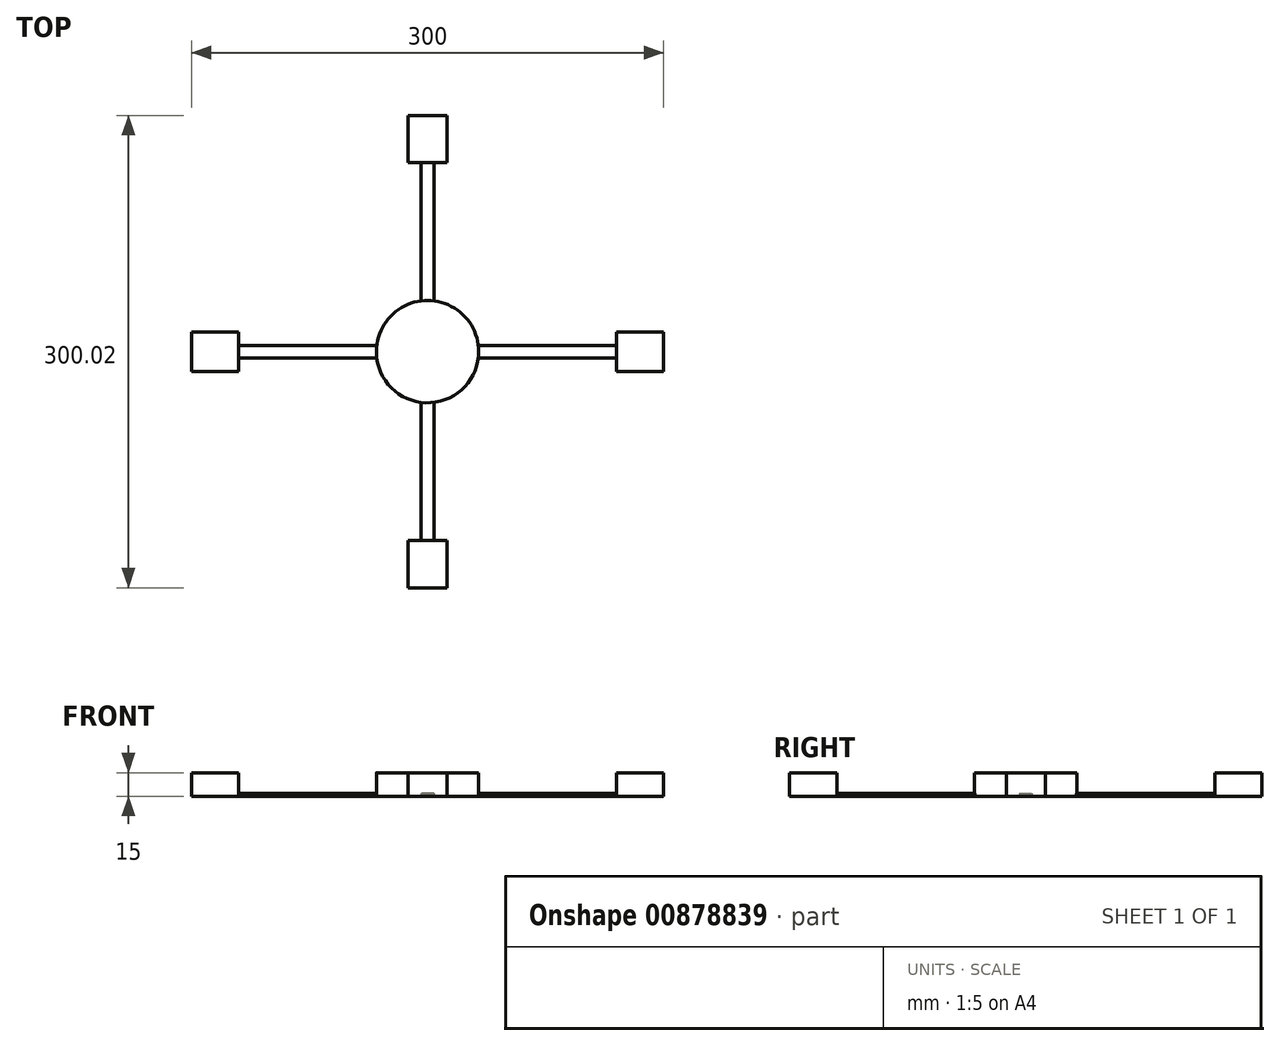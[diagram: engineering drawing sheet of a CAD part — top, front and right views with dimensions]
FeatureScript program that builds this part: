
annotation { "Feature Type Name" : "Feature", "Feature Type Description" : "" }
export const myFeature = defineFeature(function(context is Context, id is Id, definition is map)
    precondition{}
    {
        {
            var Q0;
            Q0=qCreatedBy(makeId("Top.planeOp"),FACE);
            var sketch = newSketch(context, id + "F0", { "sketchPlane" : qUnion([Q0])});
            skLineSegment(sketch, "E0.bottom", {"start": v(-120, -12.5) * mm, "end": v(-150, -12.5) * mm});
            skLineSegment(sketch, "E0.top", {"start": v(-120, 12.5) * mm, "end": v(-150, 12.5) * mm});
            skLineSegment(sketch, "E0.left", {"start": v(-120, -12.5) * mm, "end": v(-120, -4) * mm});
            skLineSegment(sketch, "E0.right", {"start": v(-150, -12.5) * mm, "end": v(-150, 12.5) * mm});
            skPoint(sketch, "E0.middle", {"position": v(-135, 0) * mm});
            skLineSegment(sketch, "E1.bottom", {"start": v(12.5, 150.02) * mm, "end": v(-12.5, 150.02) * mm});
            skLineSegment(sketch, "E1.top", {"start": v(12.5, 120.02) * mm, "end": v(4, 120.02) * mm});
            skLineSegment(sketch, "E1.left", {"start": v(12.5, 150.02) * mm, "end": v(12.5, 120.02) * mm});
            skLineSegment(sketch, "E1.right", {"start": v(-12.5, 150.02) * mm, "end": v(-12.5, 120.02) * mm});
            skPoint(sketch, "E1.middle", {"position": v(0, 135.02) * mm});
            skLineSegment(sketch, "E2.bottom", {"start": v(150, -12.5) * mm, "end": v(120, -12.5) * mm});
            skLineSegment(sketch, "E2.top", {"start": v(150, 12.5) * mm, "end": v(120, 12.5) * mm});
            skLineSegment(sketch, "E2.left", {"start": v(150, -12.5) * mm, "end": v(150, 12.5) * mm});
            skLineSegment(sketch, "E2.right", {"start": v(120, -12.5) * mm, "end": v(120, -4) * mm});
            skPoint(sketch, "E2.middle", {"position": v(135, 0) * mm});
            skLineSegment(sketch, "E3.bottom", {"start": v(12.5, -150) * mm, "end": v(-12.5, -150) * mm});
            skLineSegment(sketch, "E3.top", {"start": v(12.5, -120) * mm, "end": v(4, -120) * mm});
            skLineSegment(sketch, "E3.left", {"start": v(12.5, -150) * mm, "end": v(12.5, -120) * mm});
            skLineSegment(sketch, "E3.right", {"start": v(-12.5, -150) * mm, "end": v(-12.5, -120) * mm});
            skPoint(sketch, "E3.middle", {"position": v(0, -135) * mm});
            skArc(sketch, "E4", {"start": v(4, -32.25) * mm, "mid": v(22.98, -22.98) * mm, "end": v(32.25, -4) * mm});
            skLineSegment(sketch, "E5.left", {"start": v(4, 32.25) * mm, "end": v(4, 120.02) * mm});
            skLineSegment(sketch, "E5.right", {"start": v(-4, 32.25) * mm, "end": v(-4, 120.02) * mm});
            skLineSegment(sketch, "E6.bottom", {"start": v(120, -4) * mm, "end": v(32.25, -4) * mm});
            skLineSegment(sketch, "E6.top", {"start": v(120, 4) * mm, "end": v(32.25, 4) * mm});
            skLineSegment(sketch, "E7.bottom", {"start": v(-32.25, -4) * mm, "end": v(-120, -4) * mm});
            skLineSegment(sketch, "E7.top", {"start": v(-32.25, 4) * mm, "end": v(-120, 4) * mm});
            skLineSegment(sketch, "E8.left", {"start": v(4, -32.25) * mm, "end": v(4, -120) * mm});
            skLineSegment(sketch, "E8.right", {"start": v(-4, -32.25) * mm, "end": v(-4, -120) * mm});
            skLineSegment(sketch, "E9.trimOffspring", {"start": v(-4, 120.02) * mm, "end": v(-12.5, 120.02) * mm});
            skArc(sketch, "E10.trimOffspring", {"start": v(-32.25, -4) * mm, "mid": v(-22.98, -22.98) * mm, "end": v(-4, -32.25) * mm});
            skArc(sketch, "E11.trimOffspring", {"start": v(32.25, 4) * mm, "mid": v(22.98, 22.98) * mm, "end": v(4, 32.25) * mm});
            skLineSegment(sketch, "E12.trimOffspring", {"start": v(-120, 4) * mm, "end": v(-120, 12.5) * mm});
            skLineSegment(sketch, "E13.trimOffspring", {"start": v(-4, -120) * mm, "end": v(-12.5, -120) * mm});
            skArc(sketch, "E14.trimOffspring", {"start": v(-4, 32.25) * mm, "mid": v(-22.98, 22.98) * mm, "end": v(-32.25, 4) * mm});
            skLineSegment(sketch, "E15.trimOffspring", {"start": v(120, 4) * mm, "end": v(120, 12.5) * mm});
            skSolve(sketch);
        }
        {
            var Q0;
            Q0=makeQuery(id+"F0.imprint","IMPRINT",FACE,{"disambiguationData":[TD([[makeQuery(id+"F0.imprint","IMPRINT",EDGE,{"derivedFrom":sQuery(id+"F0.wireOp",EDGE,"E0.bottom")}),-1.0]])]});
            extrude(context, id + "F1", {"entities" : qUnion([Q0]), "depth" : 2 * mm, "offsetDistance" : 25 * mm});
        }
        {
            var Q0;
            Q0=makeQuery(id+"F1.opExtrude","CAP_FACE",FACE,{"disambiguationData":[OSD([sQuery(id+"F0.wireOp",EDGE,"E0.bottom"),sQuery(id+"F0.wireOp",EDGE,"E0.top"),sQuery(id+"F0.wireOp",EDGE,"E0.left"),sQuery(id+"F0.wireOp",EDGE,"E0.right"),sQuery(id+"F0.wireOp",EDGE,"E1.bottom"),sQuery(id+"F0.wireOp",EDGE,"E1.top"),sQuery(id+"F0.wireOp",EDGE,"E1.left"),sQuery(id+"F0.wireOp",EDGE,"E1.right"),sQuery(id+"F0.wireOp",EDGE,"E2.bottom"),sQuery(id+"F0.wireOp",EDGE,"E2.top"),sQuery(id+"F0.wireOp",EDGE,"E2.left"),sQuery(id+"F0.wireOp",EDGE,"E2.right"),sQuery(id+"F0.wireOp",EDGE,"E3.bottom"),sQuery(id+"F0.wireOp",EDGE,"E3.top"),sQuery(id+"F0.wireOp",EDGE,"E3.left"),sQuery(id+"F0.wireOp",EDGE,"E3.right"),sQuery(id+"F0.wireOp",EDGE,"E4"),sQuery(id+"F0.wireOp",EDGE,"E5.left"),sQuery(id+"F0.wireOp",EDGE,"E5.right"),sQuery(id+"F0.wireOp",EDGE,"E6.bottom"),sQuery(id+"F0.wireOp",EDGE,"E6.top"),sQuery(id+"F0.wireOp",EDGE,"E7.bottom"),sQuery(id+"F0.wireOp",EDGE,"E7.top"),sQuery(id+"F0.wireOp",EDGE,"E8.left"),sQuery(id+"F0.wireOp",EDGE,"E8.right"),sQuery(id+"F0.wireOp",EDGE,"E9.trimOffspring"),sQuery(id+"F0.wireOp",EDGE,"E10.trimOffspring"),sQuery(id+"F0.wireOp",EDGE,"E11.trimOffspring"),sQuery(id+"F0.wireOp",EDGE,"E12.trimOffspring"),sQuery(id+"F0.wireOp",EDGE,"E13.trimOffspring"),sQuery(id+"F0.wireOp",EDGE,"E14.trimOffspring"),sQuery(id+"F0.wireOp",EDGE,"E15.trimOffspring")])],"isStart":false});
            var sketch = newSketch(context, id + "F2", { "sketchPlane" : qUnion([Q0])});
            skCircle(sketch, "E16", {"center": v(0, 0) * mm, "radius": 32.5 * mm});
            skLineSegment(sketch, "E17.bottom", {"start": v(-120, 12.5) * mm, "end": v(-150, 12.5) * mm});
            skLineSegment(sketch, "E17.top", {"start": v(-120, -12.5) * mm, "end": v(-150, -12.5) * mm});
            skLineSegment(sketch, "E17.left", {"start": v(-120, 12.5) * mm, "end": v(-120, -12.5) * mm});
            skLineSegment(sketch, "E17.right", {"start": v(-150, 12.5) * mm, "end": v(-150, -12.5) * mm});
            skPoint(sketch, "E17.middle", {"position": v(-135, 0) * mm});
            skPoint(sketch, "E17.middle.positionSnap0", {"position": v(-150, 0) * mm});
            skPoint(sketch, "E17.middle.positionSnap1", {"position": v(-135, 12.5) * mm});
            skPoint(sketch, "E17.centerSnap0", {"position": v(-150, 0) * mm});
            skPoint(sketch, "E17.centerSnap1", {"position": v(-135, 12.5) * mm});
            skLineSegment(sketch, "E18.bottom", {"start": v(12.5, -120) * mm, "end": v(-12.5, -120) * mm});
            skLineSegment(sketch, "E18.top", {"start": v(12.5, -150) * mm, "end": v(-12.5, -150) * mm});
            skLineSegment(sketch, "E18.left", {"start": v(12.5, -120) * mm, "end": v(12.5, -150) * mm});
            skLineSegment(sketch, "E18.right", {"start": v(-12.5, -120) * mm, "end": v(-12.5, -150) * mm});
            skPoint(sketch, "E18.middle", {"position": v(0, -135) * mm});
            skPoint(sketch, "E18.middle.positionSnap0", {"position": v(0, -150) * mm});
            skPoint(sketch, "E18.middle.positionSnap1", {"position": v(-12.5, -135) * mm});
            skPoint(sketch, "E18.centerSnap0", {"position": v(0, -150) * mm});
            skPoint(sketch, "E18.centerSnap1", {"position": v(-12.5, -135) * mm});
            skLineSegment(sketch, "E19.bottom", {"start": v(120, -12.5) * mm, "end": v(150, -12.5) * mm});
            skLineSegment(sketch, "E19.top", {"start": v(120, 12.5) * mm, "end": v(150, 12.5) * mm});
            skLineSegment(sketch, "E19.left", {"start": v(120, -12.5) * mm, "end": v(120, 12.5) * mm});
            skLineSegment(sketch, "E19.right", {"start": v(150, -12.5) * mm, "end": v(150, 12.5) * mm});
            skPoint(sketch, "E19.middle", {"position": v(135, 0) * mm});
            skPoint(sketch, "E19.middle.positionSnap0", {"position": v(150, 0) * mm});
            skPoint(sketch, "E19.middle.positionSnap1", {"position": v(135, 12.5) * mm});
            skPoint(sketch, "E19.centerSnap0", {"position": v(150, 0) * mm});
            skPoint(sketch, "E19.centerSnap1", {"position": v(135, 12.5) * mm});
            skLineSegment(sketch, "E20.bottom", {"start": v(12.5, 120.02) * mm, "end": v(-12.5, 120.02) * mm});
            skLineSegment(sketch, "E20.top", {"start": v(12.5, 150.02) * mm, "end": v(-12.5, 150.02) * mm});
            skLineSegment(sketch, "E20.left", {"start": v(12.5, 120.02) * mm, "end": v(12.5, 150.02) * mm});
            skLineSegment(sketch, "E20.right", {"start": v(-12.5, 120.02) * mm, "end": v(-12.5, 150.02) * mm});
            skPoint(sketch, "E20.middle", {"position": v(0, 135.02) * mm});
            skPoint(sketch, "E20.middle.positionSnap0", {"position": v(12.5, 135.02) * mm});
            skPoint(sketch, "E20.middle.positionSnap1", {"position": v(0, 150.02) * mm});
            skPoint(sketch, "E20.centerSnap0", {"position": v(12.5, 135.02) * mm});
            skPoint(sketch, "E20.centerSnap1", {"position": v(0, 150.02) * mm});
            skSolve(sketch);
        }
        {
            var Q0;
            Q0 = qSketchRegion(id + "F2", true);
            extrude(context, id + "F3", {"entities" : qUnion([Q0]), "operationType" : NewBodyOperationType.ADD, "depth" : 13 * mm, "offsetDistance" : 25 * mm});
        }
    });
